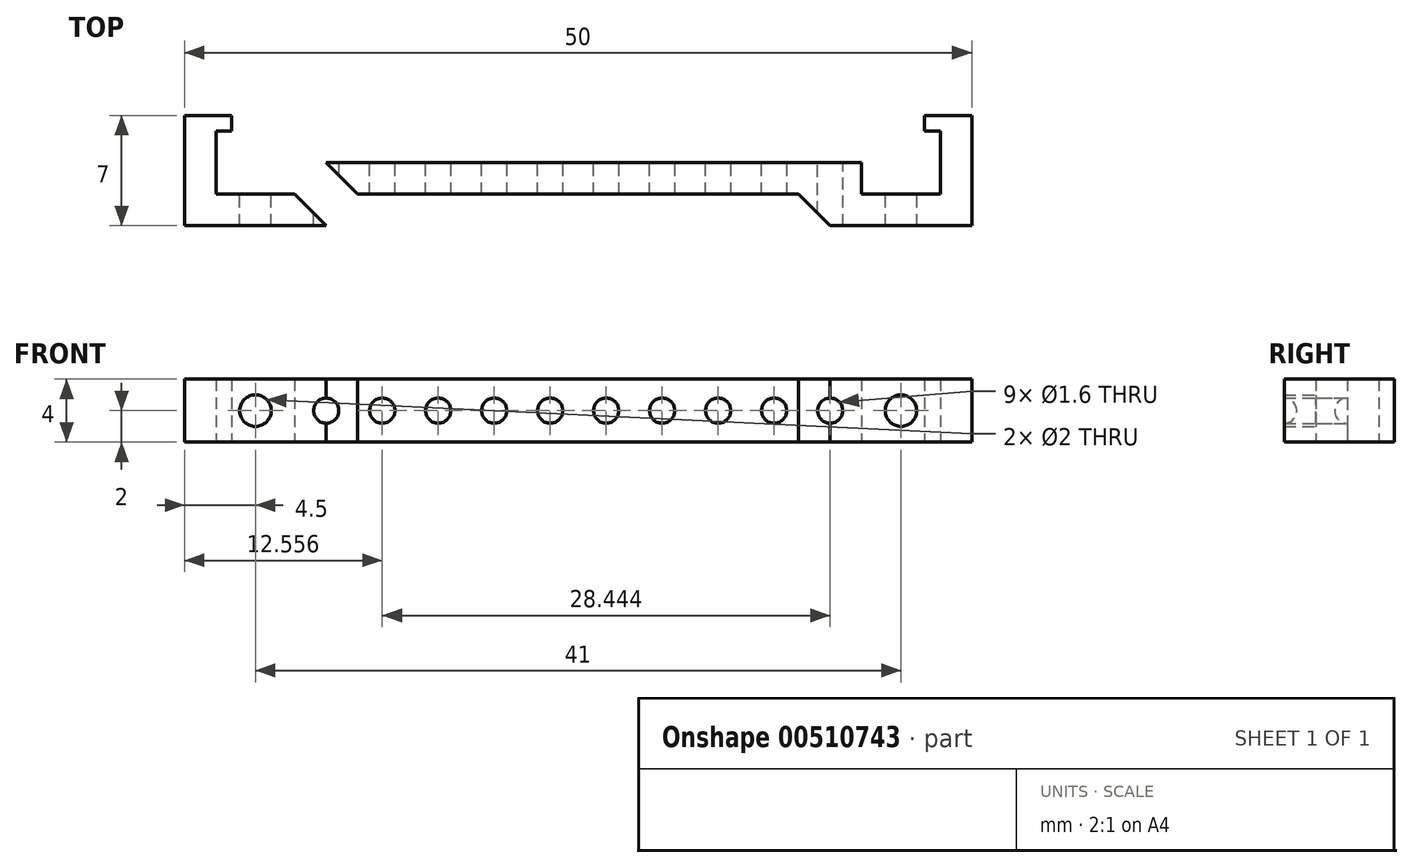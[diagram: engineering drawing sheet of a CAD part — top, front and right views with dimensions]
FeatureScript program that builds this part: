
annotation { "Feature Type Name" : "Feature", "Feature Type Description" : "" }
export const myFeature = defineFeature(function(context is Context, id is Id, definition is map)
    precondition{}
    {
        {
            var Q0;
            Q0=qCreatedBy(makeId("Top.planeOp"),FACE);
            var sketch = newSketch(context, id + "F0", { "sketchPlane" : qUnion([Q0])});
            skLineSegment(sketch, "E0.bottom", {"start": v(0, 0) * mm, "end": v(2, 0) * mm});
            skLineSegment(sketch, "E0.top", {"start": v(0, -5) * mm, "end": v(2, -5) * mm});
            skLineSegment(sketch, "E0.left", {"start": v(0, 0) * mm, "end": v(0, -5) * mm});
            skLineSegment(sketch, "E0.right", {"start": v(2, 0) * mm, "end": v(2, -5) * mm});
            skLineSegment(sketch, "E1.bottom", {"start": v(0, -5) * mm, "end": v(7, -5) * mm});
            skLineSegment(sketch, "E1.top", {"start": v(0, -7) * mm, "end": v(7, -7) * mm});
            skLineSegment(sketch, "E1.left", {"start": v(0, -5) * mm, "end": v(0, -7) * mm});
            skLineSegment(sketch, "E1.right", {"start": v(7, -5) * mm, "end": v(7, -7) * mm});
            skLineSegment(sketch, "E2.bottom", {"start": v(7, -7) * mm, "end": v(9, -7) * mm});
            skLineSegment(sketch, "E2.top", {"start": v(7, -3) * mm, "end": v(9, -3) * mm});
            skLineSegment(sketch, "E2.left", {"start": v(7, -7) * mm, "end": v(7, -3) * mm});
            skLineSegment(sketch, "E2.right", {"start": v(9, -7) * mm, "end": v(9, -3) * mm});
            skLineSegment(sketch, "E3.bottom", {"start": v(2, 0) * mm, "end": v(3, 0) * mm});
            skLineSegment(sketch, "E3.top", {"start": v(2, -1) * mm, "end": v(3, -1) * mm});
            skLineSegment(sketch, "E3.left", {"start": v(2, 0) * mm, "end": v(2, -1) * mm});
            skLineSegment(sketch, "E3.right", {"start": v(3, 0) * mm, "end": v(3, -1) * mm});
            skLineSegment(sketch, "E4.bottom", {"start": v(7, -3) * mm, "end": v(25, -3) * mm});
            skLineSegment(sketch, "E4.top", {"start": v(7, -5) * mm, "end": v(25, -5) * mm});
            skLineSegment(sketch, "E4.left", {"start": v(7, -3) * mm, "end": v(7, -5) * mm});
            skLineSegment(sketch, "E4.right", {"start": v(25, -3) * mm, "end": v(25, -5) * mm});
            skLineSegment(sketch, "E5.MirrorCS", {"start": v(47, 0) * mm, "end": v(47, -1) * mm});
            skLineSegment(sketch, "E6.MirrorCS", {"start": v(48, 0) * mm, "end": v(48, -1) * mm});
            skLineSegment(sketch, "E7.MirrorCS", {"start": v(50, -5) * mm, "end": v(48, -5) * mm});
            skLineSegment(sketch, "E8.MirrorCS", {"start": v(43, -3) * mm, "end": v(41, -3) * mm});
            skLineSegment(sketch, "E9.MirrorCS", {"start": v(43, -5) * mm, "end": v(43, -7) * mm});
            skLineSegment(sketch, "E10.MirrorCS", {"start": v(50, 0) * mm, "end": v(48, 0) * mm});
            skLineSegment(sketch, "E11.MirrorCS", {"start": v(50, -5) * mm, "end": v(50, -7) * mm});
            skLineSegment(sketch, "E12.MirrorCS", {"start": v(48, 0) * mm, "end": v(48, -5) * mm});
            skLineSegment(sketch, "E13.MirrorCS", {"start": v(50, 0) * mm, "end": v(50, -5) * mm});
            skLineSegment(sketch, "E14.MirrorCS", {"start": v(43, -3) * mm, "end": v(43, -5) * mm});
            skLineSegment(sketch, "E15.MirrorCS", {"start": v(43, -7) * mm, "end": v(41, -7) * mm});
            skLineSegment(sketch, "E16.MirrorCS", {"start": v(43, -7) * mm, "end": v(43, -3) * mm});
            skLineSegment(sketch, "E17.MirrorCS", {"start": v(48, -1) * mm, "end": v(47, -1) * mm});
            skLineSegment(sketch, "E18.MirrorCS", {"start": v(48, 0) * mm, "end": v(47, 0) * mm});
            skLineSegment(sketch, "E19.MirrorCS", {"start": v(41, -7) * mm, "end": v(41, -3) * mm});
            skLineSegment(sketch, "E20.MirrorCS", {"start": v(50, -5) * mm, "end": v(43, -5) * mm});
            skLineSegment(sketch, "E21.MirrorCS", {"start": v(43, -5) * mm, "end": v(25, -5) * mm});
            skLineSegment(sketch, "E22.MirrorCS", {"start": v(50, -7) * mm, "end": v(43, -7) * mm});
            skLineSegment(sketch, "E23.MirrorCS", {"start": v(43, -3) * mm, "end": v(25, -3) * mm});
            skSolve(sketch);
        }
        {
            var Q0;
            {var subQ0=sQuery(id+"F0.wireOp",EDGE,"E4.right");Q0=makeQuery(id+"F0.imprint","IMPRINT",FACE,{"disambiguationData":[TD([[makeQuery(id+"F0.imprint","IMPRINT",EDGE,{"derivedFrom":subQ0}),1.0]])]});}
            var Q1;
            {var subQ5=sQuery(id+"F0.wireOp",EDGE,"E4.right");Q1=makeQuery(id+"F0.imprint","IMPRINT",FACE,{"disambiguationData":[TD([[makeQuery(id+"F0.imprint","IMPRINT",EDGE,{"derivedFrom":subQ5}),-1.0]])]});}
            var Q2;
            {var subQ4=sQuery(id+"F0.wireOp",EDGE,"E11.MirrorCS");Q2=makeQuery(id+"F0.imprint","IMPRINT",FACE,{"disambiguationData":[TD([[makeQuery(id+"F0.imprint","IMPRINT",EDGE,{"derivedFrom":subQ4}),-1.0]])]});}
            var Q3;
            {var subQ0=sQuery(id+"F0.wireOp",EDGE,"E15.MirrorCS");Q3=makeQuery(id+"F0.imprint","IMPRINT",FACE,{"disambiguationData":[TD([[makeQuery(id+"F0.imprint","IMPRINT",EDGE,{"derivedFrom":subQ0}),-1.0]])]});}
            var Q4;
            Q4=makeQuery(id+"F0.imprint","IMPRINT",FACE,{"disambiguationData":[TD([[makeQuery(id+"F0.imprint","IMPRINT",EDGE,{"derivedFrom":sQuery(id+"F0.wireOp",EDGE,"E1.top")}),1.0]])]});
            var Q5;
            Q5=makeQuery(id+"F0.imprint","IMPRINT",FACE,{"disambiguationData":[TD([[makeQuery(id+"F0.imprint","IMPRINT",EDGE,{"derivedFrom":sQuery(id+"F0.wireOp",EDGE,"E0.bottom")}),-1.0]])]});
            var Q6;
            Q6=makeQuery(id+"F0.imprint","IMPRINT",FACE,{"disambiguationData":[TD([[makeQuery(id+"F0.imprint","IMPRINT",EDGE,{"derivedFrom":sQuery(id+"F0.wireOp",EDGE,"E5.MirrorCS")}),1.0]])]});
            var Q7;
            {var subQ5=sQuery(id+"F0.wireOp",EDGE,"E4.left");Q7=makeQuery(id+"F0.imprint","IMPRINT",FACE,{"disambiguationData":[TD([[makeQuery(id+"F0.imprint","IMPRINT",EDGE,{"derivedFrom":subQ5}),1.0]])]});}
            var Q8;
            {var subQ0=sQuery(id+"F0.wireOp",EDGE,"E2.bottom");Q8=makeQuery(id+"F0.imprint","IMPRINT",FACE,{"disambiguationData":[TD([[makeQuery(id+"F0.imprint","IMPRINT",EDGE,{"derivedFrom":subQ0}),1.0]])]});}
            var Q9;
            Q9=makeQuery(id+"F0.imprint","IMPRINT",FACE,{"disambiguationData":[TD([[makeQuery(id+"F0.imprint","IMPRINT",EDGE,{"derivedFrom":sQuery(id+"F0.wireOp",EDGE,"E3.bottom")}),-1.0]])]});
            var Q10;
            {var subQ0=sQuery(id+"F0.wireOp",EDGE,"E23.MirrorCS");var subQ5=sQuery(id+"F0.wireOp",EDGE,"E19.MirrorCS");var subQ6=makeQuery(id+"F0.imprint","INTERSECT",VERTEX,{"derivedFrom":[subQ5,subQ0]});Q10=makeQuery(id+"F0.imprint","IMPRINT",FACE,{"disambiguationData":[TD([[makeQuery(id+"F0.imprint","IMPRINT",EDGE,{"disambiguationData":[TD([[subQ6,1.0]])],"derivedFrom":subQ5}),-1.0]])]});}
            var Q11;
            {var subQ5=sQuery(id+"F0.wireOp",EDGE,"E10.MirrorCS");Q11=makeQuery(id+"F0.imprint","IMPRINT",FACE,{"disambiguationData":[TD([[makeQuery(id+"F0.imprint","IMPRINT",EDGE,{"derivedFrom":subQ5}),1.0]])]});}
            extrude(context, id + "F1", {"entities" : qUnion([Q0, Q1, Q2, Q3, Q4, Q5, Q6, Q7, Q8, Q9, Q10, Q11]), "depth" : 4 * mm});
        }
        {
            var Q0;
            Q0=makeQuery(id+"F1.opExtrude","SWEPT_EDGE",EDGE,{"disambiguationData":[OSD([sQuery(id+"F0.wireOp",EDGE,"E19.MirrorCS"),sQuery(id+"F0.wireOp",EDGE,"E21.MirrorCS")])]});
            var Q1;
            Q1=makeQuery(id+"F1.opExtrude","SWEPT_EDGE",EDGE,{"disambiguationData":[OSD([sQuery(id+"F0.wireOp",EDGE,"E2.right"),sQuery(id+"F0.wireOp",EDGE,"E4.top")])]});
            chamfer(context, id + "F2", {"entities" : qUnion([Q0, Q1]), "width" : 2 * mm, "tangentPropagation" : true});
        }
        {
            var Q0;
            Q0=makeQuery(id+"F1.opExtrude","SWEPT_FACE",FACE,{"disambiguationData":[OSD([sQuery(id+"F0.wireOp",EDGE,"E20.MirrorCS")])]});
            var sketch = newSketch(context, id + "F3", { "sketchPlane" : qUnion([Q0])});
            skCircle(sketch, "E24", {"center": v(-4.5, 2) * mm, "radius": 1 * mm});
            skPoint(sketch, "E24.centerSnap0", {"position": v(-2, 2) * mm});
            skPoint(sketch, "E24.centerSnap1", {"position": v(-4.5, 4) * mm});
            skCircle(sketch, "E25", {"center": v(-45.5, 2) * mm, "radius": 1 * mm});
            skPoint(sketch, "E25.centerSnap0", {"position": v(-45.5, 4) * mm});
            skPoint(sketch, "E25.centerSnap1", {"position": v(-48, 2) * mm});
            skSolve(sketch);
        }
        {
            var Q0;
            Q0=makeQuery(id+"F3.imprint","IMPRINT",FACE,{"disambiguationData":[TD([[makeQuery(id+"F3.imprint","IMPRINT",EDGE,{"derivedFrom":sQuery(id+"F3.wireOp",EDGE,"E24")}),1.0]])]});
            var Q1;
            Q1=makeQuery(id+"F3.imprint","IMPRINT",FACE,{"disambiguationData":[TD([[makeQuery(id+"F3.imprint","IMPRINT",EDGE,{"derivedFrom":sQuery(id+"F3.wireOp",EDGE,"E25")}),1.0]])]});
            extrude(context, id + "F4", {"entities" : qUnion([Q0, Q1]), "operationType" : NewBodyOperationType.REMOVE, "oppositeDirection" : true, "depth" : 2 * mm});
        }
        {
            var Q0;
            Q0=makeQuery(id+"F1.opExtrude","SWEPT_FACE",FACE,{"disambiguationData":[OSD([sQuery(id+"F0.wireOp",EDGE,"E4.bottom"),sQuery(id+"F0.wireOp",EDGE,"E23.MirrorCS")])]});
            var sketch = newSketch(context, id + "F5", { "sketchPlane" : qUnion([Q0])});
            skCircle(sketch, "E26", {"center": v(-9, 2) * mm, "radius": 0.8 * mm});
            skPoint(sketch, "E26.centerSnap0", {"position": v(-7, 2) * mm});
            skCircle(sketch, "E27.1.0.0", {"center": v(-12.56, 2) * mm, "radius": 0.8 * mm});
            skCircle(sketch, "E27.2.0.0", {"center": v(-16.11, 2) * mm, "radius": 0.8 * mm});
            skLineSegment(sketch, "E27.direction1", {"start": v(-9, 2) * mm, "end": v(-12.56, 2) * mm, "construction": true});
            skCircle(sketch, "E28.0.3.0", {"center": v(-19.67, 2) * mm, "radius": 0.8 * mm});
            skCircle(sketch, "E28.0.4.0", {"center": v(-23.22, 2) * mm, "radius": 0.8 * mm});
            skCircle(sketch, "E28.0.5.0", {"center": v(-26.78, 2) * mm, "radius": 0.8 * mm});
            skCircle(sketch, "E28.0.6.0", {"center": v(-30.33, 2) * mm, "radius": 0.8 * mm});
            skCircle(sketch, "E28.0.7.0", {"center": v(-33.89, 2) * mm, "radius": 0.8 * mm});
            skCircle(sketch, "E29.0.8.0", {"center": v(-37.44, 2) * mm, "radius": 0.8 * mm});
            skCircle(sketch, "E30.0.9.0", {"center": v(-41, 2) * mm, "radius": 0.8 * mm});
            skSolve(sketch);
        }
        {
            var Q0;
            Q0=makeQuery(id+"F5.imprint","IMPRINT",FACE,{"disambiguationData":[TD([[makeQuery(id+"F5.imprint","IMPRINT",EDGE,{"derivedFrom":sQuery(id+"F5.wireOp",EDGE,"E27.2.0.0")}),1.0]])]});
            var Q1;
            Q1=makeQuery(id+"F5.imprint","IMPRINT",FACE,{"disambiguationData":[TD([[makeQuery(id+"F5.imprint","IMPRINT",EDGE,{"derivedFrom":sQuery(id+"F5.wireOp",EDGE,"E26")}),1.0]])]});
            var Q2;
            Q2=makeQuery(id+"F5.imprint","IMPRINT",FACE,{"disambiguationData":[TD([[makeQuery(id+"F5.imprint","IMPRINT",EDGE,{"derivedFrom":sQuery(id+"F5.wireOp",EDGE,"E27.1.0.0")}),1.0]])]});
            var Q3;
            Q3=makeQuery(id+"F5.imprint","IMPRINT",FACE,{"disambiguationData":[TD([[makeQuery(id+"F5.imprint","IMPRINT",EDGE,{"derivedFrom":sQuery(id+"F5.wireOp",EDGE,"E28.0.3.0")}),1.0]])]});
            var Q4;
            Q4=makeQuery(id+"F5.imprint","IMPRINT",FACE,{"disambiguationData":[TD([[makeQuery(id+"F5.imprint","IMPRINT",EDGE,{"derivedFrom":sQuery(id+"F5.wireOp",EDGE,"E28.0.4.0")}),1.0]])]});
            var Q5;
            Q5=makeQuery(id+"F5.imprint","IMPRINT",FACE,{"disambiguationData":[TD([[makeQuery(id+"F5.imprint","IMPRINT",EDGE,{"derivedFrom":sQuery(id+"F5.wireOp",EDGE,"E28.0.5.0")}),1.0]])]});
            var Q6;
            Q6=makeQuery(id+"F5.imprint","IMPRINT",FACE,{"disambiguationData":[TD([[makeQuery(id+"F5.imprint","IMPRINT",EDGE,{"derivedFrom":sQuery(id+"F5.wireOp",EDGE,"E28.0.6.0")}),1.0]])]});
            var Q7;
            Q7=makeQuery(id+"F5.imprint","IMPRINT",FACE,{"disambiguationData":[TD([[makeQuery(id+"F5.imprint","IMPRINT",EDGE,{"derivedFrom":sQuery(id+"F5.wireOp",EDGE,"E28.0.7.0")}),1.0]])]});
            var Q8;
            Q8=makeQuery(id+"F5.imprint","IMPRINT",FACE,{"disambiguationData":[TD([[makeQuery(id+"F5.imprint","IMPRINT",EDGE,{"derivedFrom":sQuery(id+"F5.wireOp",EDGE,"E29.0.8.0")}),1.0]])]});
            var Q9;
            Q9=makeQuery(id+"F5.imprint","IMPRINT",FACE,{"disambiguationData":[TD([[makeQuery(id+"F5.imprint","IMPRINT",EDGE,{"derivedFrom":sQuery(id+"F5.wireOp",EDGE,"E30.0.9.0")}),1.0]])]});
            extrude(context, id + "F6", {"entities" : qUnion([Q0, Q1, Q2, Q3, Q4, Q5, Q6, Q7, Q8, Q9]), "operationType" : NewBodyOperationType.REMOVE, "oppositeDirection" : true, "depth" : 5 * mm});
        }
    });
